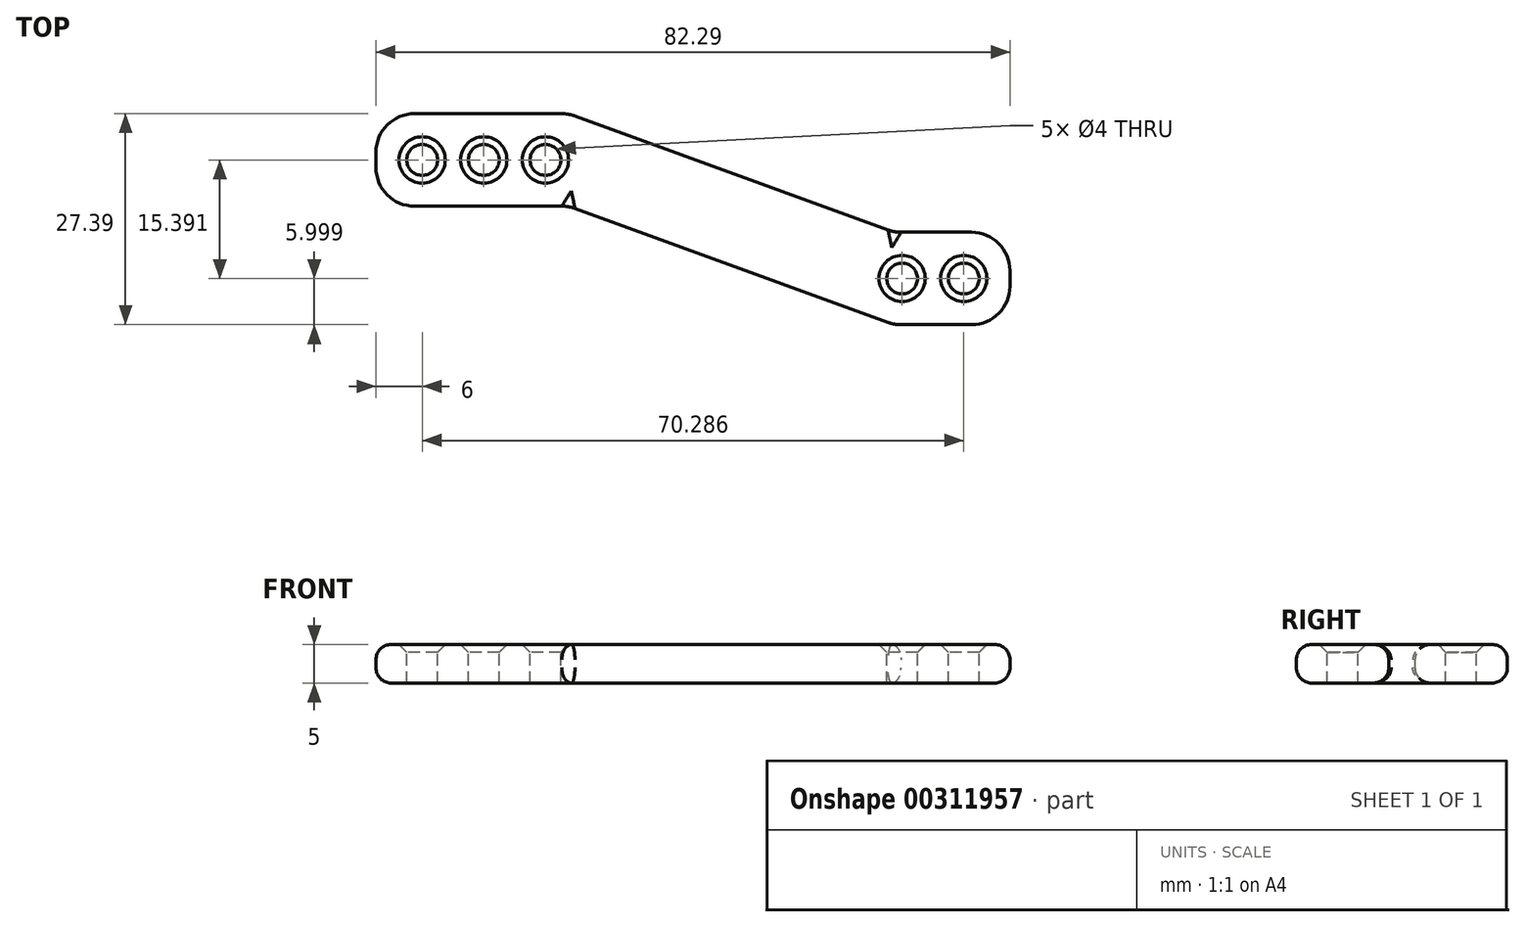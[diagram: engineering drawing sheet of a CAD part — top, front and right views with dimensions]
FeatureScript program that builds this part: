
annotation { "Feature Type Name" : "Feature", "Feature Type Description" : "" }
export const myFeature = defineFeature(function(context is Context, id is Id, definition is map)
    precondition{}
    {
        {
            var Q0;
            Q0=qCreatedBy(makeId("Top.planeOp"),FACE);
            var sketch = newSketch(context, id + "F0", { "sketchPlane" : qUnion([Q0])});
            skLineSegment(sketch, "E0.bottom", {"start": v(0, 0) * mm, "end": v(25, 0) * mm});
            skLineSegment(sketch, "E0.top", {"start": v(0, 12) * mm, "end": v(25, 12) * mm});
            skLineSegment(sketch, "E0.left", {"start": v(0, 0) * mm, "end": v(0, 12) * mm});
            skLineSegment(sketch, "E0.right", {"start": v(25, 0) * mm, "end": v(25, 12) * mm});
            skLineSegment(sketch, "E1.bottom", {"start": v(67.29, -3.4) * mm, "end": v(82.29, -3.4) * mm});
            skLineSegment(sketch, "E1.top", {"start": v(67.29, -15.4) * mm, "end": v(82.29, -15.4) * mm});
            skLineSegment(sketch, "E1.left", {"start": v(67.29, -3.4) * mm, "end": v(67.29, -15.4) * mm});
            skLineSegment(sketch, "E1.right", {"start": v(82.29, -3.4) * mm, "end": v(82.29, -15.4) * mm});
            skLineSegment(sketch, "E2", {"start": v(25, 0) * mm, "end": v(67.29, -15.4) * mm});
            skLineSegment(sketch, "E3", {"start": v(67.29, -3.4) * mm, "end": v(25, 12) * mm});
            skSolve(sketch);
        }
        {
            var Q0;
            Q0=makeQuery(id+"F0.imprint","IMPRINT",FACE,{"disambiguationData":[TD([[makeQuery(id+"F0.imprint","IMPRINT",EDGE,{"derivedFrom":sQuery(id+"F0.wireOp",EDGE,"E0.bottom")}),1.0]])]});
            var Q1;
            Q1=makeQuery(id+"F0.imprint","IMPRINT",FACE,{"disambiguationData":[TD([[makeQuery(id+"F0.imprint","IMPRINT",EDGE,{"derivedFrom":sQuery(id+"F0.wireOp",EDGE,"E0.right")}),-1.0]])]});
            var Q2;
            Q2=makeQuery(id+"F0.imprint","IMPRINT",FACE,{"disambiguationData":[TD([[makeQuery(id+"F0.imprint","IMPRINT",EDGE,{"derivedFrom":sQuery(id+"F0.wireOp",EDGE,"E1.bottom")}),-1.0]])]});
            extrude(context, id + "F1", {"entities" : qUnion([Q0, Q1, Q2]), "depth" : 5 * mm});
        }
        {
            var Q0;
            Q0=makeQuery(id+"F1.opExtrude","CAP_FACE",FACE,{"disambiguationData":[OSD([sQuery(id+"F0.wireOp",EDGE,"E0.bottom"),sQuery(id+"F0.wireOp",EDGE,"E0.top"),sQuery(id+"F0.wireOp",EDGE,"E0.left"),sQuery(id+"F0.wireOp",EDGE,"E1.bottom"),sQuery(id+"F0.wireOp",EDGE,"E1.top"),sQuery(id+"F0.wireOp",EDGE,"E1.right"),sQuery(id+"F0.wireOp",EDGE,"E2"),sQuery(id+"F0.wireOp",EDGE,"E3")])],"isStart":false});
            var sketch = newSketch(context, id + "F2", { "sketchPlane" : qUnion([Q0])});
            skCircle(sketch, "E4", {"center": v(6, 6) * mm, "radius": 2 * mm});
            skCircle(sketch, "E5", {"center": v(76.29, -9.4) * mm, "radius": 2 * mm});
            skCircle(sketch, "E6.1.0.0", {"center": v(14, 6) * mm, "radius": 2 * mm});
            skCircle(sketch, "E6.2.0.0", {"center": v(22, 6) * mm, "radius": 2 * mm});
            skLineSegment(sketch, "E6.direction1", {"start": v(6, 6) * mm, "end": v(14, 6) * mm, "construction": true});
            skCircle(sketch, "E7.1.0.0", {"center": v(68.29, -9.4) * mm, "radius": 2 * mm});
            skLineSegment(sketch, "E7.direction1", {"start": v(76.29, -9.4) * mm, "end": v(68.29, -9.4) * mm, "construction": true});
            skSolve(sketch);
        }
        {
            var Q0;
            Q0 = qSketchRegion(id + "F2", true);
            extrude(context, id + "F3", {"entities" : qUnion([Q0]), "operationType" : NewBodyOperationType.REMOVE, "endBound" : BoundingType.THROUGH_ALL, "oppositeDirection" : true, "depth" : 5 * mm});
        }
        {
            var Q0;
            Q0=makeQuery(id+"F1.opExtrude","CAP_EDGE",EDGE,{"disambiguationData":[OSD([sQuery(id+"F0.wireOp",EDGE,"E3")])],"isStart":false});
            var Q1;
            Q1=makeQuery(id+"F1.opExtrude","CAP_EDGE",EDGE,{"disambiguationData":[OSD([sQuery(id+"F0.wireOp",EDGE,"E0.top")])],"isStart":false});
            var Q2;
            Q2=makeQuery(id+"F1.opExtrude","CAP_EDGE",EDGE,{"disambiguationData":[OSD([sQuery(id+"F0.wireOp",EDGE,"E1.bottom")])],"isStart":false});
            var Q3;
            Q3=makeQuery(id+"F1.opExtrude","CAP_EDGE",EDGE,{"disambiguationData":[OSD([sQuery(id+"F0.wireOp",EDGE,"E1.right")])],"isStart":false});
            var Q4;
            Q4=makeQuery(id+"F1.opExtrude","CAP_EDGE",EDGE,{"disambiguationData":[OSD([sQuery(id+"F0.wireOp",EDGE,"E1.top")])],"isStart":false});
            var Q5;
            Q5=makeQuery(id+"F1.opExtrude","CAP_EDGE",EDGE,{"disambiguationData":[OSD([sQuery(id+"F0.wireOp",EDGE,"E2")])],"isStart":false});
            var Q6;
            Q6=makeQuery(id+"F1.opExtrude","CAP_EDGE",EDGE,{"disambiguationData":[OSD([sQuery(id+"F0.wireOp",EDGE,"E0.left")])],"isStart":false});
            var Q7;
            Q7=makeQuery(id+"F1.opExtrude","CAP_EDGE",EDGE,{"disambiguationData":[OSD([sQuery(id+"F0.wireOp",EDGE,"E0.bottom")])],"isStart":false});
            var Q8;
            Q8=makeQuery(id+"F1.opExtrude","CAP_EDGE",EDGE,{"disambiguationData":[OSD([sQuery(id+"F0.wireOp",EDGE,"E1.bottom")])],"isStart":true});
            var Q9;
            Q9=makeQuery(id+"F1.opExtrude","CAP_EDGE",EDGE,{"disambiguationData":[OSD([sQuery(id+"F0.wireOp",EDGE,"E1.right")])],"isStart":true});
            var Q10;
            Q10=makeQuery(id+"F1.opExtrude","CAP_EDGE",EDGE,{"disambiguationData":[OSD([sQuery(id+"F0.wireOp",EDGE,"E1.top")])],"isStart":true});
            var Q11;
            Q11=makeQuery(id+"F1.opExtrude","CAP_EDGE",EDGE,{"disambiguationData":[OSD([sQuery(id+"F0.wireOp",EDGE,"E2")])],"isStart":true});
            var Q12;
            Q12=makeQuery(id+"F1.opExtrude","CAP_EDGE",EDGE,{"disambiguationData":[OSD([sQuery(id+"F0.wireOp",EDGE,"E3")])],"isStart":true});
            var Q13;
            Q13=makeQuery(id+"F1.opExtrude","CAP_EDGE",EDGE,{"disambiguationData":[OSD([sQuery(id+"F0.wireOp",EDGE,"E0.top")])],"isStart":true});
            var Q14;
            Q14=makeQuery(id+"F1.opExtrude","CAP_EDGE",EDGE,{"disambiguationData":[OSD([sQuery(id+"F0.wireOp",EDGE,"E0.left")])],"isStart":true});
            var Q15;
            Q15=makeQuery(id+"F1.opExtrude","CAP_EDGE",EDGE,{"disambiguationData":[OSD([sQuery(id+"F0.wireOp",EDGE,"E0.bottom")])],"isStart":true});
            fillet(context, id + "F4", {"entities" : qUnion([Q0, Q1, Q2, Q3, Q4, Q5, Q6, Q7, Q8, Q9, Q10, Q11, Q12, Q13, Q14, Q15]), "radius" : 2 * mm, "tangentPropagation" : true, "allowEdgeOverflow" : false});
        }
        {
            var Q0;
            Q0=makeQuery(id+"F1.opExtrude","SWEPT_EDGE",EDGE,{"disambiguationData":[OSD([sQuery(id+"F0.wireOp",EDGE,"E1.top"),sQuery(id+"F0.wireOp",EDGE,"E1.right")])]});
            var Q1;
            Q1=makeQuery(id+"F1.opExtrude","SWEPT_EDGE",EDGE,{"disambiguationData":[OSD([sQuery(id+"F0.wireOp",EDGE,"E1.top"),sQuery(id+"F0.wireOp",EDGE,"E1.left"),sQuery(id+"F0.wireOp",EDGE,"E2")])]});
            var Q2;
            Q2=makeQuery(id+"F1.opExtrude","SWEPT_EDGE",EDGE,{"disambiguationData":[OSD([sQuery(id+"F0.wireOp",EDGE,"E0.bottom"),sQuery(id+"F0.wireOp",EDGE,"E0.right"),sQuery(id+"F0.wireOp",EDGE,"E2")])]});
            var Q3;
            Q3=makeQuery(id+"F1.opExtrude","SWEPT_EDGE",EDGE,{"disambiguationData":[OSD([sQuery(id+"F0.wireOp",EDGE,"E0.bottom"),sQuery(id+"F0.wireOp",EDGE,"E0.left")])]});
            var Q4;
            Q4=makeQuery(id+"F1.opExtrude","SWEPT_EDGE",EDGE,{"disambiguationData":[OSD([sQuery(id+"F0.wireOp",EDGE,"E0.top"),sQuery(id+"F0.wireOp",EDGE,"E0.left")])]});
            var Q5;
            Q5=makeQuery(id+"F1.opExtrude","SWEPT_EDGE",EDGE,{"disambiguationData":[OSD([sQuery(id+"F0.wireOp",EDGE,"E0.top"),sQuery(id+"F0.wireOp",EDGE,"E0.right"),sQuery(id+"F0.wireOp",EDGE,"E3")])]});
            var Q6;
            Q6=makeQuery(id+"F1.opExtrude","SWEPT_EDGE",EDGE,{"disambiguationData":[OSD([sQuery(id+"F0.wireOp",EDGE,"E1.bottom"),sQuery(id+"F0.wireOp",EDGE,"E1.left"),sQuery(id+"F0.wireOp",EDGE,"E3")])]});
            var Q7;
            Q7=makeQuery(id+"F1.opExtrude","SWEPT_EDGE",EDGE,{"disambiguationData":[OSD([sQuery(id+"F0.wireOp",EDGE,"E1.bottom"),sQuery(id+"F0.wireOp",EDGE,"E1.right")])]});
            fillet(context, id + "F5", {"entities" : qUnion([Q0, Q1, Q2, Q3, Q4, Q5, Q6, Q7]), "radius" : 5 * mm, "tangentPropagation" : true, "allowEdgeOverflow" : false});
        }
        {
            var Q0;
            Q0=makeQuery(id+"F1.opExtrude","CAP_FACE",FACE,{"disambiguationData":[OSD([sQuery(id+"F0.wireOp",EDGE,"E0.bottom"),sQuery(id+"F0.wireOp",EDGE,"E0.top"),sQuery(id+"F0.wireOp",EDGE,"E0.left"),sQuery(id+"F0.wireOp",EDGE,"E1.bottom"),sQuery(id+"F0.wireOp",EDGE,"E1.top"),sQuery(id+"F0.wireOp",EDGE,"E1.right"),sQuery(id+"F0.wireOp",EDGE,"E2"),sQuery(id+"F0.wireOp",EDGE,"E3")])],"isStart":false});
            chamfer(context, id + "F6", {"entities" : qUnion([Q0]), "width" : 1 * mm, "tangentPropagation" : true});
        }
    });
